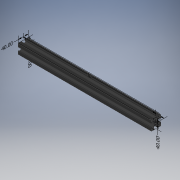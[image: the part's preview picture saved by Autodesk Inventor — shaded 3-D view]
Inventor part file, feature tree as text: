
AUTODESK INVENTOR PART (.ipt)
format: ipt  version: 2019 (Build 230136000, 136)  size: 275,456 bytes
history: native  units: mm
features: other x125, extrude x1, sketch x1
ambient origin geometry x8: Origin, YZ Plane, XZ Plane, XY Plane, X Axis, Y Axis, Z Axis, Center Point
bodies: Solid1 (feature_tree)
feature tree (127):
  other  "Annotations"
  extrude  "Extrusion1"  [1 undecoded]
  other  "CS_ANBAU_HINTEN_LINKS_XY"
  other  "CS_ANBAU_HINTEN_LINKS_YZ"
  other  "CS_ANBAU_HINTEN_LINKS_ZX"
  other  "CS_ANBAU_HINTEN_LINKS_X"
  other  "CS_ANBAU_HINTEN_LINKS_Y"
  other  "CS_ANBAU_HINTEN_LINKS_Z"
  other  "CS_ANBAU_HINTEN_LINKS_Center"
  other  "CS_ANBAU_HINTEN_OBEN_XY"
  other  "CS_ANBAU_HINTEN_OBEN_YZ"
  other  "CS_ANBAU_HINTEN_OBEN_ZX"
  other  "CS_ANBAU_HINTEN_OBEN_X"
  other  "CS_ANBAU_HINTEN_OBEN_Y"
  other  "CS_ANBAU_HINTEN_OBEN_Z"
  other  "CS_ANBAU_HINTEN_OBEN_Center"
  other  "CS_ANBAU_HINTEN_RECHTS_XY"
  other  "CS_ANBAU_HINTEN_RECHTS_YZ"
  other  "CS_ANBAU_HINTEN_RECHTS_ZX"
  other  "CS_ANBAU_HINTEN_RECHTS_X"
  other  "CS_ANBAU_HINTEN_RECHTS_Y"
  other  "CS_ANBAU_HINTEN_RECHTS_Z"
  other  "CS_ANBAU_HINTEN_RECHTS_Center"
  other  "CS_ANBAU_HINTEN_UNTEN_XY"
  other  "CS_ANBAU_HINTEN_UNTEN_YZ"
  other  "CS_ANBAU_HINTEN_UNTEN_ZX"
  other  "CS_ANBAU_HINTEN_UNTEN_X"
  other  "CS_ANBAU_HINTEN_UNTEN_Y"
  other  "CS_ANBAU_HINTEN_UNTEN_Z"
  other  "CS_ANBAU_HINTEN_UNTEN_Center"
  other  "CS_ANBAU_QUER_XY"
  other  "CS_ANBAU_QUER_YZ"
  other  "CS_ANBAU_QUER_ZX"
  other  "CS_ANBAU_QUER_X"
  other  "CS_ANBAU_QUER_Y"
  other  "CS_ANBAU_QUER_Z"
  other  "CS_ANBAU_QUER_Center"
  other  "CS_ANBAU_QUER_1_XY"
  other  "CS_ANBAU_QUER_1_YZ"
  other  "CS_ANBAU_QUER_1_ZX"
  other  "CS_ANBAU_QUER_1_X"
  other  "CS_ANBAU_QUER_1_Y"
  other  "CS_ANBAU_QUER_1_Z"
  other  "CS_ANBAU_QUER_1_Center"
  other  "CS_ANBAU_VORNE_LINKS_XY"
  other  "CS_ANBAU_VORNE_LINKS_YZ"
  other  "CS_ANBAU_VORNE_LINKS_ZX"
  other  "CS_ANBAU_VORNE_LINKS_X"
  other  "CS_ANBAU_VORNE_LINKS_Y"
  other  "CS_ANBAU_VORNE_LINKS_Z"
  other  "CS_ANBAU_VORNE_LINKS_Center"
  other  "CS_ANBAU_VORNE_OBEN_XY"
  other  "CS_ANBAU_VORNE_OBEN_YZ"
  other  "CS_ANBAU_VORNE_OBEN_ZX"
  other  "CS_ANBAU_VORNE_OBEN_X"
  other  "CS_ANBAU_VORNE_OBEN_Y"
  other  "CS_ANBAU_VORNE_OBEN_Z"
  other  "CS_ANBAU_VORNE_OBEN_Center"
  other  "CS_ANBAU_VORNE_RECHTS_XY"
  other  "CS_ANBAU_VORNE_RECHTS_YZ"
  other  "CS_ANBAU_VORNE_RECHTS_ZX"
  other  "CS_ANBAU_VORNE_RECHTS_X"
  other  "CS_ANBAU_VORNE_RECHTS_Y"
  other  "CS_ANBAU_VORNE_RECHTS_Z"
  other  "CS_ANBAU_VORNE_RECHTS_Center"
  other  "CS_ANBAU_VORNE_UNTEN_XY"
  other  "CS_ANBAU_VORNE_UNTEN_YZ"
  other  "CS_ANBAU_VORNE_UNTEN_ZX"
  other  "CS_ANBAU_VORNE_UNTEN_X"
  other  "CS_ANBAU_VORNE_UNTEN_Y"
  other  "CS_ANBAU_VORNE_UNTEN_Z"
  other  "CS_ANBAU_VORNE_UNTEN_Center"
  other  "p1_XY"
  other  "p1_YZ"
  other  "p1_ZX"
  other  "p1_X"
  other  "p1_Y"
  other  "p1_Z"
  other  "p1_Center"
  other  "p2_XY"
  other  "p2_YZ"
  other  "p2_ZX"
  other  "p2_X"
  other  "p2_Y"
  other  "p2_Z"
  other  "p2_Center"
  other  "p3_XY"
  other  "p3_YZ"
  other  "p3_ZX"
  other  "p3_X"
  other  "p3_Y"
  other  "p3_Z"
  other  "p3_Center"
  other  "p4_XY"
  other  "p4_YZ"
  other  "p4_ZX"
  other  "p4_X"
  other  "p4_Y"
  other  "p4_Z"
  other  "p4_Center"
  other  "p5_XY"
  other  "p5_YZ"
  other  "p5_ZX"
  other  "p5_X"
  other  "p5_Y"
  other  "p5_Z"
  other  "p5_Center"
  other  "pm1_XY"
  other  "pm1_YZ"
  other  "pm1_ZX"
  other  "pm1_X"
  other  "pm1_Y"
  other  "pm1_Z"
  other  "pm1_Center"
  other  "pm2_XY"
  other  "pm2_YZ"
  other  "pm2_ZX"
  other  "pm2_X"
  other  "pm2_Y"
  other  "pm2_Z"
  other  "pm2_Center"
  sketch  "Skizze_1"  dims[d0=540.0mm d1=0.0mm d2=0.0mm d3=0.0mm d4=0.0mm d5=0.0mm d6=0.0mm d10=540.0mm d11=540.0mm d7=40.0mm d8=40.0mm d9=40.0mm]
  other  "Linear Dimension 1"
  other  "Linear Dimension 2"
  other  "Linear Dimension 3"
  other  "Linear Dimension 4"
  other  "Linear Dimension 5"
note: 1 required parameter value undecoded (feature->parameter linkage not recoverable at this tier; creation-order binding heuristic only, values carry confidence <= 0.55)
